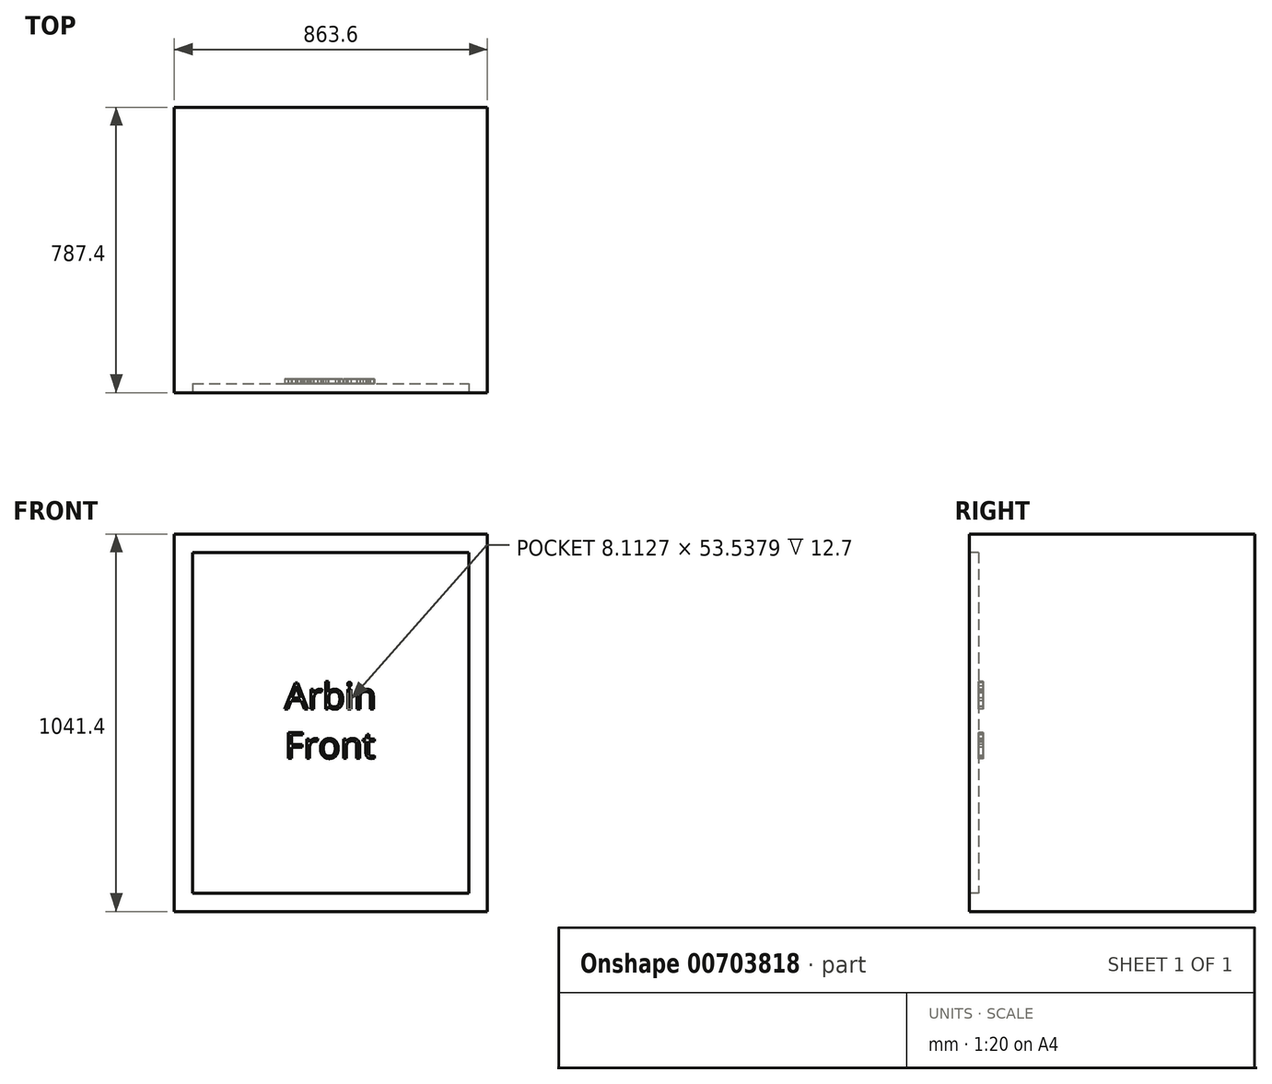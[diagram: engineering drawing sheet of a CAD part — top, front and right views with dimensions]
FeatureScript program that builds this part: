
annotation { "Feature Type Name" : "Feature", "Feature Type Description" : "" }
export const myFeature = defineFeature(function(context is Context, id is Id, definition is map)
    precondition{}
    {
        {
            var Q0;
            Q0=qCreatedBy(makeId("Top.planeOp"),FACE);
            var sketch = newSketch(context, id + "F0", { "sketchPlane" : qUnion([Q0])});
            skLineSegment(sketch, "E0.bottom", {"start": v(431.8, -393.7) * mm, "end": v(-431.8, -393.7) * mm});
            skLineSegment(sketch, "E0.top", {"start": v(431.8, 393.7) * mm, "end": v(-431.8, 393.7) * mm});
            skLineSegment(sketch, "E0.left", {"start": v(431.8, -393.7) * mm, "end": v(431.8, 393.7) * mm});
            skLineSegment(sketch, "E0.right", {"start": v(-431.8, -393.7) * mm, "end": v(-431.8, 393.7) * mm});
            skPoint(sketch, "E0.middle", {"position": v(0, 0) * mm});
            skSolve(sketch);
        }
        {
            var Q0;
            Q0 = qSketchRegion(id + "F0", true);
            extrude(context, id + "F1", {"entities" : qUnion([Q0]), "depth" : 1041.4 * mm, "offsetDistance" : 25.4 * mm});
        }
        {
            var Q0;
            Q0=makeQuery(id+"F1.opExtrude","SWEPT_FACE",FACE,{"disambiguationData":[OSD([sQuery(id+"F0.wireOp",EDGE,"E0.bottom")])]});
            var sketch = newSketch(context, id + "F2", { "sketchPlane" : qUnion([Q0])});
            skLineSegment(sketch, "E1.bottom", {"start": v(-381, 990.6) * mm, "end": v(381, 990.6) * mm});
            skLineSegment(sketch, "E1.top", {"start": v(-381, 50.8) * mm, "end": v(381, 50.8) * mm});
            skLineSegment(sketch, "E1.left", {"start": v(-381, 990.6) * mm, "end": v(-381, 50.8) * mm});
            skLineSegment(sketch, "E1.right", {"start": v(381, 990.6) * mm, "end": v(381, 50.8) * mm});
            skSolve(sketch);
        }
        {
            var Q0;
            Q0 = qSketchRegion(id + "F2", true);
            extrude(context, id + "F3", {"entities" : qUnion([Q0]), "operationType" : NewBodyOperationType.REMOVE, "oppositeDirection" : true, "depth" : 25.4 * mm, "offsetDistance" : 25.4 * mm});
        }
        {
            var Q0;
            Q0=makeQuery(id+"F3.boolean.opBoolean","COPY",FACE,{"derivedFrom":makeQuery(id+"F3.opExtrude","CAP_FACE",FACE,{"disambiguationData":[OSD([sQuery(id+"F2.wireOp",EDGE,"E1.bottom"),sQuery(id+"F2.wireOp",EDGE,"E1.top"),sQuery(id+"F2.wireOp",EDGE,"E1.left"),sQuery(id+"F2.wireOp",EDGE,"E1.right")])],"isStart":false})});
            var sketch = newSketch(context, id + "F4", { "sketchPlane" : qUnion([Q0])});
            skText(sketch, "E2", { "text": "Arbin \nFront\n", "fontName": "OpenSans-Regular.ttf"});
            const initialGuessF4  = {"E2": [-0.127, 0.5588, 1, 0, 0.07203]};
            skSetInitialGuess(sketch, initialGuessF4);
            skSolve(sketch);
        }
        {
            var Q0;
            Q0 = qSketchRegion(id + "F4", true);
            extrude(context, id + "F5", {"entities" : qUnion([Q0]), "operationType" : NewBodyOperationType.REMOVE, "oppositeDirection" : true, "depth" : 12.7 * mm, "offsetDistance" : 25.4 * mm});
        }
    });
